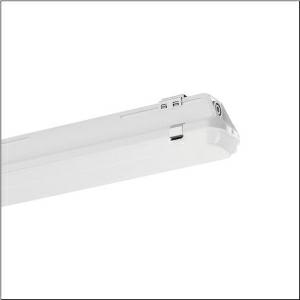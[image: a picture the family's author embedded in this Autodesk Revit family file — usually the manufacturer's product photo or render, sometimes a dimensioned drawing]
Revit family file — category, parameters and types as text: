
# Revit family: monsun_11_51fp209p460h
name_source: partatom
category: Lighting Fixtures
units: mm (PartAtom-declared; Revit-internal decimal feet)

## family parameters
Cut with Voids When Loaded = No
Host = Face
Light Source = No
Part Type = Normal
Room Calculation Point = No
Round Connector Dimension = Use Diameter
Shared = No

## types (1)
- Monsun 11 (1 x LED, 5490 lm, 34 W, 4000K)
    Apparent Load = 34 VA
    CIE Flux Codes = 45 75 93 94 100
    Color Rendering = 80
    Color Temperature = 4000K
    Default Elevation = 1800 mm
    Description = Monsun 11, damp-proof luminaire, chain hanger, primary optical cover: enclosure, of PC, light emission: direct distribution, primary light characteristic: symmetric, installation type: suspended mounting, surface-mounted, horizontal mounting, vertical mounting, LED, rated luminous flux: 5.490lm, luminous efficacy: 161lm/W, light colour: 840, colour temperature: 4000K, control gear: ON/OFF, with terminal, 3-pole, max. 2.5mm², mains connection: 220..240V, AC, 50/60Hz, rated input power: 34W, luminaire housing, of glass-fibre reinforced polyester, uncoated, bright grey, incl. chain hanger, length: 1.590mm, width: 90mm, height: 88mm, clip for enclosure, of stainless steel (V2A), ceiling mounting element, of stainless steel (V2A), chain hanger, of stainless steel (V2A), protection rating (complete): IP66, insulation class (complete): insulation class I (protective earthing), certification: CE, ENEC, VDE, UKCA, protection symbol: D, impact resistance: IK08, permissible operating ambient temperature: -35..+40°C, standard: EN 50419, EN 60598-2-1, no direct snow, no direct sun, no direct rain, for indoor or canopied outdoor use, corresponds to IFS (International Featured Standards) requirements for safety and quality in the food industry, contact your sales advisor before using the luminaires in applications with unclear chemical exposure, large temperature fluctuations or condensation-forming humidity, LABS conformity tested according to VDMA 24364:2018-05, packaging unit: 1 piece
    Height = 89 mm
    Lamp = 1 x LED
    Lamp Light Flux = 5490 lm
    Lamp Power = 34 W
    Lamp count = 1
    Length = 1590 mm
    Luminous efficacy = 161 lm/W
    Manufacturer = Siteco
    ModVariant = No
    Model = 51FP209P460H
    Mounting Place = Ceiling
    Mounting Type = Surface mounted
    Number of Poles = 1
    OnlyDefault = Yes
    Power Factor = 1
    Product Name = Monsun 11
    Product group = damp-proof luminaire
    ProductGroupID = 300
    Protection Class = Protection class I
    Protection Degree = IP 66
    RLX_Detail_Level = 1
    RLX_Emergency_Light_Flux = 0 lm
    RLX_Emergency_Type = 0
    RLX_Emergency_Type_DB = No
    RlxData = <blob elided: 88493 chars, md5=fbe76b43>
    Socket = socket
    Standby Power = 0 W
    System Light Flux = 5490 lm
    System Power = 34 W
    Type Comments = Product without accessories
    Type Image = l_1349237.jpg
    URL = http://relux.com
    VarID = ---
    Voltage = 0 V
    Weight = 0.00 kg
    Width = 90 mm

## geometry (parser evidence)
native form markers: Blend x4, Sweep x11
no freeform markers — native parametric forms only
